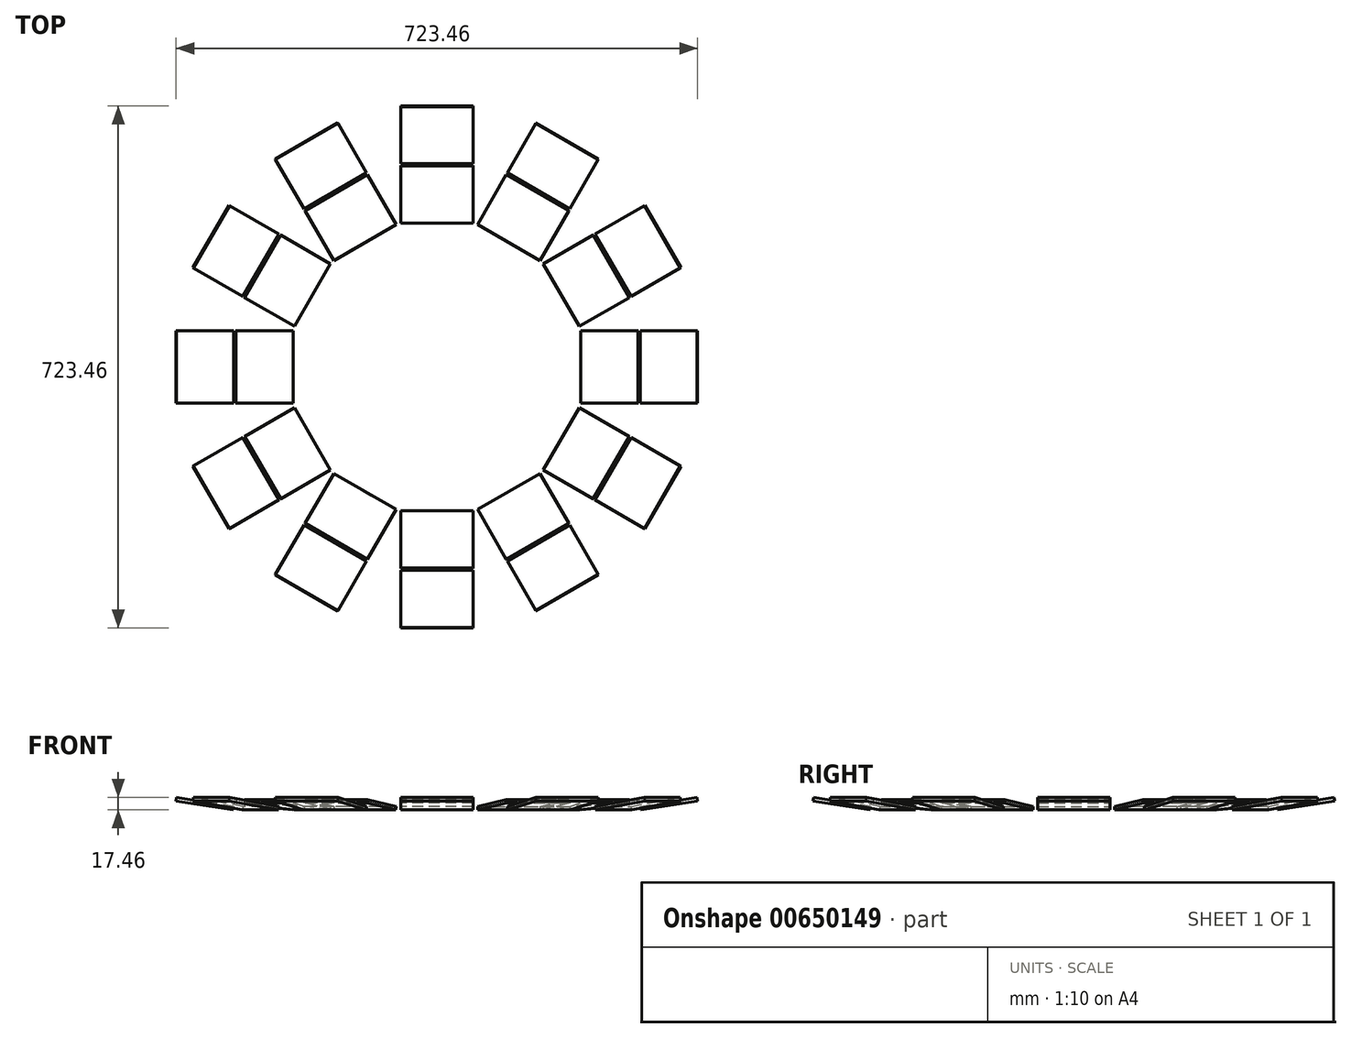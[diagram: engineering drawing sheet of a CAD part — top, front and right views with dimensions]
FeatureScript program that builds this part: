
annotation { "Feature Type Name" : "Feature", "Feature Type Description" : "" }
export const myFeature = defineFeature(function(context is Context, id is Id, definition is map)
    precondition{}
    {
        {
            assignVariable(context, id + "F0", {"name" : "r", "anyValue" : 200});
        }
        {
            assignVariable(context, id + "F1", {"name" : "w", "anyValue" : 100});
        }
        {
            var Q0;
            Q0=qCreatedBy(makeId("Right.planeOp"),FACE);
            var sketch = newSketch(context, id + "F2", { "sketchPlane" : qUnion([Q0])});
            skLineSegment(sketch, "E0", {"start": v(0, 0) * mm, "end": v(0, 1000) * mm, "construction": true});
            skLineSegment(sketch, "E1.bottom", {"start": v(199.4, 4.96) * mm, "end": v(278.85, 14.42) * mm});
            skLineSegment(sketch, "E1.top", {"start": v(200, 0) * mm, "end": v(279.44, 9.46) * mm});
            skLineSegment(sketch, "E1.left", {"start": v(199.4, 4.96) * mm, "end": v(200, 0) * mm});
            skLineSegment(sketch, "E1.right", {"start": v(278.85, 14.42) * mm, "end": v(279.44, 9.46) * mm});
            skLineSegment(sketch, "E2", {"start": v(0, 0) * mm, "end": v(1000, 0) * mm});
            skLineSegment(sketch, "E3", {"start": v(239.13, 9.7) * mm, "end": v(121.26, 1000) * mm, "construction": true});
            skLineSegment(sketch, "E4", {"start": v(0, 1000) * mm, "end": v(239.13, 9.7) * mm, "construction": true});
            skLineSegment(sketch, "E5", {"start": v(239.13, 9.7) * mm, "end": v(239.13, 1000) * mm, "construction": true});
            skLineSegment(sketch, "E6.bottom", {"start": v(281.93, 4.94) * mm, "end": v(360.94, 17.46) * mm});
            skLineSegment(sketch, "E6.top", {"start": v(282.71, 0) * mm, "end": v(361.73, 12.52) * mm});
            skLineSegment(sketch, "E6.left", {"start": v(281.93, 4.94) * mm, "end": v(282.71, 0) * mm});
            skLineSegment(sketch, "E6.right", {"start": v(360.94, 17.46) * mm, "end": v(361.73, 12.52) * mm});
            skLineSegment(sketch, "E7", {"start": v(384.07, -384.07) * mm, "end": v(321.44, 11.2) * mm, "construction": true});
            skLineSegment(sketch, "E8", {"start": v(321.44, 11.2) * mm, "end": v(321.44, 1000) * mm, "construction": true});
            skLineSegment(sketch, "E9", {"start": v(321.44, 11.2) * mm, "end": v(0, 1000) * mm, "construction": true});
            skLineSegment(sketch, "E10", {"start": v(281.93, 4.94) * mm, "end": v(278.85, 14.42) * mm, "construction": true});
            skPoint(sketch, "E11", {"position": v(500, 0) * mm});
            skSolve(sketch);
        }
        {
            var Q0;
            Q0=makeQuery(id+"F2.imprint","IMPRINT",FACE,{"disambiguationData":[TD([[makeQuery(id+"F2.imprint","IMPRINT",EDGE,{"derivedFrom":sQuery(id+"F2.wireOp",EDGE,"E1.bottom")}),-1.0]])]});
            extrude(context, id + "F3", {"entities" : qUnion([Q0]), "endBound" : BoundingType.SYMMETRIC, "depth" : 100 * mm, "offsetDistance" : 25 * mm});
        }
        {
            var Q0;
            Q0=makeQuery(id+"F2.imprint","IMPRINT",FACE,{"disambiguationData":[TD([[makeQuery(id+"F2.imprint","IMPRINT",EDGE,{"derivedFrom":sQuery(id+"F2.wireOp",EDGE,"E6.bottom")}),-1.0]])]});
            extrude(context, id + "F4", {"entities" : qUnion([Q0]), "endBound" : BoundingType.SYMMETRIC, "depth" : 100 * mm, "offsetDistance" : 25 * mm});
        }
        {
            var Q0;
            Q0=makeQuery(id+"F3.opExtrude","SWEPT_BODY",BODY,{"disambiguationData":[OSD([sQuery(id+"F2.wireOp",EDGE,"E1.bottom"),sQuery(id+"F2.wireOp",EDGE,"E1.top"),sQuery(id+"F2.wireOp",EDGE,"E1.left"),sQuery(id+"F2.wireOp",EDGE,"E1.right")])]});
            var Q1;
            Q1=sQuery(id+"F2.wireOp",EDGE,"E0");
            circularPattern(context, id + "F5", {"entities" : qUnion([Q0]), "axis" : qUnion([Q1]), "angle" : 360 * degree, "instanceCount" : 2 * 3 * getVariable(context, 'r') / getVariable(context, 'w'), "equalSpace" : true});
        }
        {
            var Q0;
            Q0=makeQuery(id+"F4.opExtrude","SWEPT_BODY",BODY,{"disambiguationData":[OSD([sQuery(id+"F2.wireOp",EDGE,"E6.bottom"),sQuery(id+"F2.wireOp",EDGE,"E6.top"),sQuery(id+"F2.wireOp",EDGE,"E6.left"),sQuery(id+"F2.wireOp",EDGE,"E6.right")])]});
            var Q1;
            Q1=sQuery(id+"F2.wireOp",EDGE,"E0");
            circularPattern(context, id + "F6", {"entities" : qUnion([Q0]), "axis" : qUnion([Q1]), "angle" : 360 * degree, "instanceCount" : 2 * 3 * getVariable(context, 'r') / getVariable(context, 'w'), "equalSpace" : true});
        }
    });
